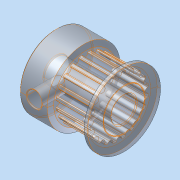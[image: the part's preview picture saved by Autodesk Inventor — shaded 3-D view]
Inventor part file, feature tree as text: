
AUTODESK INVENTOR PART (.ipt)
format: ipt  version: 2015 (Build 190159000, 159)  size: 1,020,928 bytes
history: native  units: in
note: dims shown in document units (in); Inventor stores cm internally (conversion verified against a paired STEP export)
features: other x3, sketch x1
ambient origin geometry x8: Origin, YZ Plane, XZ Plane, XY Plane, X Axis, Y Axis, Z Axis, Center Point
bodies: Body1 (feature_tree), Body2 (feature_tree), Body3 (feature_tree), Body4 (feature_tree), Body5 (feature_tree), Body6 (feature_tree), Body7 (feature_tree), Body8 (feature_tree), Body9 (feature_tree), Body10 (feature_tree), Body11 (feature_tree), Body12 (feature_tree), Body13 (feature_tree), Body14 (feature_tree), Body15 (feature_tree), Body16 (feature_tree), Body17 (feature_tree), Body18 (feature_tree), Body19 (feature_tree), Body20 (feature_tree), Body21 (feature_tree), Body22 (feature_tree), Body23 (feature_tree), Body24 (feature_tree), Body25 (feature_tree), Body26 (feature_tree), Body27 (feature_tree), Body28 (feature_tree), Body29 (feature_tree), Body30 (feature_tree), Body31 (feature_tree), Body32 (feature_tree), Body33 (feature_tree), Body34 (feature_tree), Body35 (feature_tree), Body36 (feature_tree), Body37 (feature_tree), Body38 (feature_tree), Body39 (feature_tree), Body40 (feature_tree), Body41 (feature_tree), Body42 (feature_tree), Body43 (feature_tree), Body44 (feature_tree), Body45 (feature_tree), Body46 (feature_tree), Body47 (feature_tree), Body48 (feature_tree), Body49 (feature_tree), Body50 (feature_tree), Body51 (feature_tree), Body52 (feature_tree), Body53 (feature_tree), Body54 (feature_tree), Body55 (feature_tree), Body56 (feature_tree), Body57 (feature_tree), Body58 (feature_tree), Body59 (feature_tree), Body60 (feature_tree), Body61 (feature_tree), Body62 (feature_tree), Body63 (feature_tree), Body64 (feature_tree), Body65 (feature_tree), Body66 (feature_tree), Body67 (feature_tree), Body68 (feature_tree), Body69 (feature_tree), Body70 (feature_tree), Body71 (feature_tree), Body72 (feature_tree), Body73 (feature_tree), Body74 (feature_tree), Body75 (feature_tree), Body76 (feature_tree), Body77 (feature_tree), Body78 (feature_tree), Body79 (feature_tree), Body80 (feature_tree), Body81 (feature_tree), Body82 (feature_tree), Body83 (feature_tree), Body84 (feature_tree), Body85 (feature_tree), Body86 (feature_tree), Body87 (feature_tree), Body88 (feature_tree), Body89 (feature_tree), Body90 (feature_tree), Body91 (feature_tree), Body92 (feature_tree), Body93 (feature_tree), Body94 (feature_tree), Body95 (feature_tree), Body96 (feature_tree), Body97 (feature_tree), Body98 (feature_tree), Body99 (feature_tree), Body100 (feature_tree), Body101 (feature_tree), Body102 (feature_tree), Body103 (feature_tree), Body104 (feature_tree), Body105 (feature_tree), Body106 (feature_tree), Body107 (feature_tree), Body108 (feature_tree), Body109 (feature_tree), Body110 (feature_tree), Body111 (feature_tree), Body112 (feature_tree), Body113 (feature_tree), Body114 (feature_tree), Body115 (feature_tree), Body116 (feature_tree), Body117 (feature_tree), Body118 (feature_tree), Body119 (feature_tree), Body120 (feature_tree), Body121 (feature_tree), Body122 (feature_tree), Body123 (feature_tree), Body124 (feature_tree), Body125 (feature_tree), Body126 (feature_tree), Body127 (feature_tree), Body128 (feature_tree), Body129 (feature_tree), Body130 (feature_tree), Body131 (feature_tree), Body132 (feature_tree), Body133 (feature_tree), Body134 (feature_tree)
feature tree (4):
  other  "GT2_20teeth_pulley1"
  sketch  "Sketch1"  dims[d0=0.315in]
  other  "Composite1"
  other  "Srf1"
